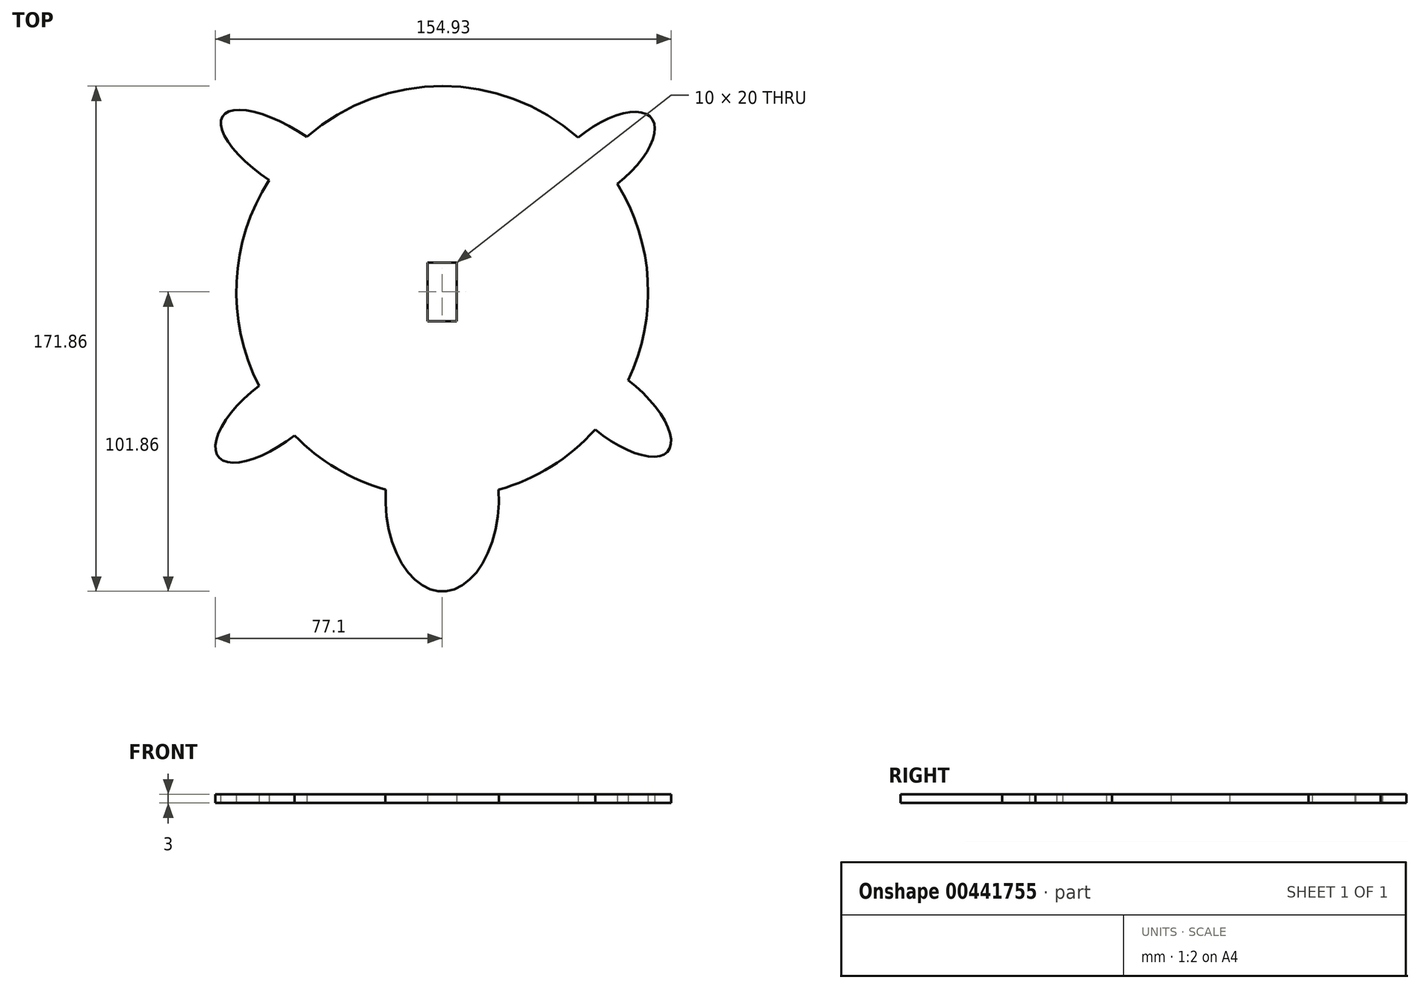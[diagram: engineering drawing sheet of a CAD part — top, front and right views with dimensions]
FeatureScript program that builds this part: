
annotation { "Feature Type Name" : "Feature", "Feature Type Description" : "" }
export const myFeature = defineFeature(function(context is Context, id is Id, definition is map)
    precondition{}
    {
        {
            var Q0;
            Q0=qCreatedBy(makeId("Top.planeOp"),FACE);
            var sketch = newSketch(context, id + "F0", { "sketchPlane" : qUnion([Q0])});
            skArc(sketch, "E0", {"start": v(-58.78, 38) * mm, "mid": v(-69.91, 3.48) * mm, "end": v(-62.26, -32) * mm});
            skLineSegment(sketch, "E1.bottom", {"start": v(-5, 10) * mm, "end": v(5, 10) * mm});
            skLineSegment(sketch, "E1.top", {"start": v(-5, -10) * mm, "end": v(5, -10) * mm});
            skLineSegment(sketch, "E1.left", {"start": v(-5, 10) * mm, "end": v(-5, -10) * mm});
            skLineSegment(sketch, "E1.right", {"start": v(5, 10) * mm, "end": v(5, -10) * mm});
            skEllipticalArc(sketch, "E2", {});
            skEllipticalArc(sketch, "E3", {});
            skEllipticalArc(sketch, "E4", {});
            skArc(sketch, "E5.trimOffspring", {"start": v(-50.2, -48.79) * mm, "mid": v(-35.92, -60.08) * mm, "end": v(-19.21, -67.31) * mm});
            skArc(sketch, "E6.trimOffspring", {"start": v(19.21, -67.31) * mm, "mid": v(65.27, -25.3) * mm, "end": v(59.57, 36.77) * mm});
            skEllipticalArc(sketch, "E7", {});
            skEllipticalArc(sketch, "E8", {});
            skArc(sketch, "E9.trimOffspring", {"start": v(46.25, 52.54) * mm, "mid": v(0.14, 70) * mm, "end": v(-46.04, 52.73) * mm});
            const initialGuessF0  = {"E2": [0, -0.07, 0, 1, 0.03185569837689399, 0.01928055282342055, 1.4863157684504849, 4.796869538729101], "E3": [-0.0568373248165974, -0.040859741894591066, -0.7844633048222768, -0.6201752360319717, 0.024499162085694373, 0.01033497075482296, 4.661564983074826, 1.582711034356735], "E4": [-0.052978829434182785, 0.045751979539510275, -0.8396828262605494, 0.5430771135696074, 0.025821256325994118, 0.009657778035419647, 4.633386756985904, 1.5449336174162442], "E7": [0.05350720784298069, 0.04513290051445912, 0.7849129323966372, 0.6196060753063288, 0.022505025629963295, 0.01032365958239066, 4.69339163190112, 1.619844734913927], "E8": [0.05820887297190683, -0.03888093501113899, 0.7711213587381828, -0.6366881890672851, 0.024049271964428406, 0.010086871678919114, 4.724624210055467, 1.6445287007117932]};
            skSetInitialGuess(sketch, initialGuessF0);
            skSolve(sketch);
        }
        {
            var Q0;
            Q0 = qSketchRegion(id + "F0", true);
            extrude(context, id + "F1", {"entities" : qUnion([Q0]), "depth" : 3 * mm});
        }
    });
